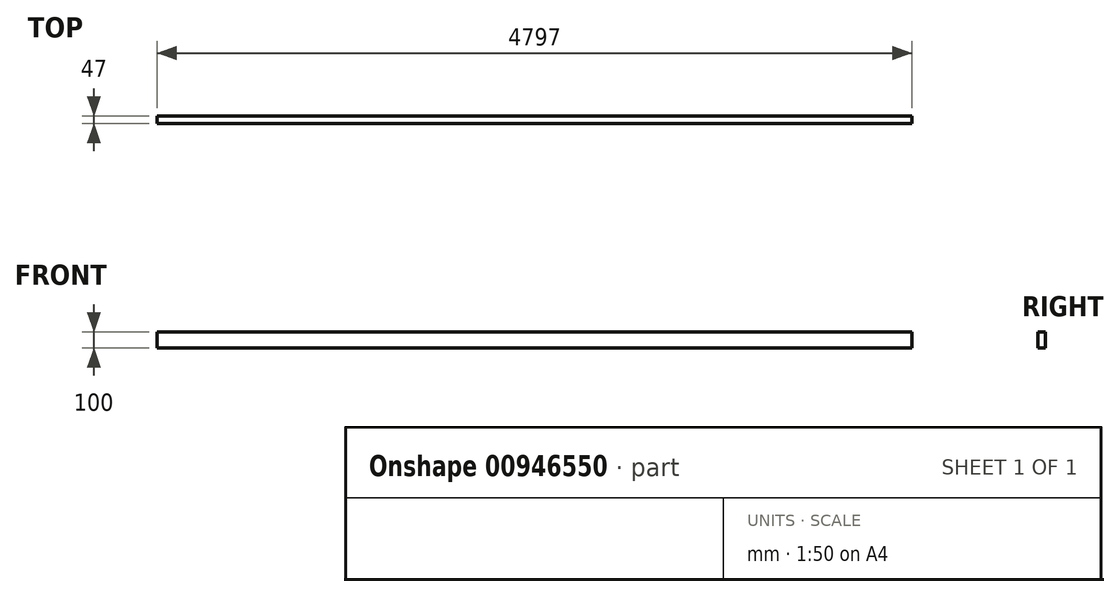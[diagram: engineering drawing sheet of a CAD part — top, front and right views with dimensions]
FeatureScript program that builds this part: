
annotation { "Feature Type Name" : "Feature", "Feature Type Description" : "" }
export const myFeature = defineFeature(function(context is Context, id is Id, definition is map)
    precondition{}
    {
        {
            var Q0;
            Q0=qCreatedBy(makeId("Right.planeOp"),FACE);
            var sketch = newSketch(context, id + "F0", { "sketchPlane" : qUnion([Q0])});
            skLineSegment(sketch, "E0.bottom", {"start": v(0, 0) * mm, "end": v(-47, 0) * mm});
            skLineSegment(sketch, "E0.top", {"start": v(0, 100) * mm, "end": v(-47, 100) * mm});
            skLineSegment(sketch, "E0.left", {"start": v(0, 0) * mm, "end": v(0, 100) * mm});
            skLineSegment(sketch, "E0.right", {"start": v(-47, 0) * mm, "end": v(-47, 100) * mm});
            skSolve(sketch);
        }
        {
            var Q0;
            Q0=qSketchRegion(id+"F0",true);
            extrude(context, id + "F1", {"entities" : qUnion([Q0]), "depth" : 4797 * mm, "offsetDistance" : 25 * mm});
        }
    });
